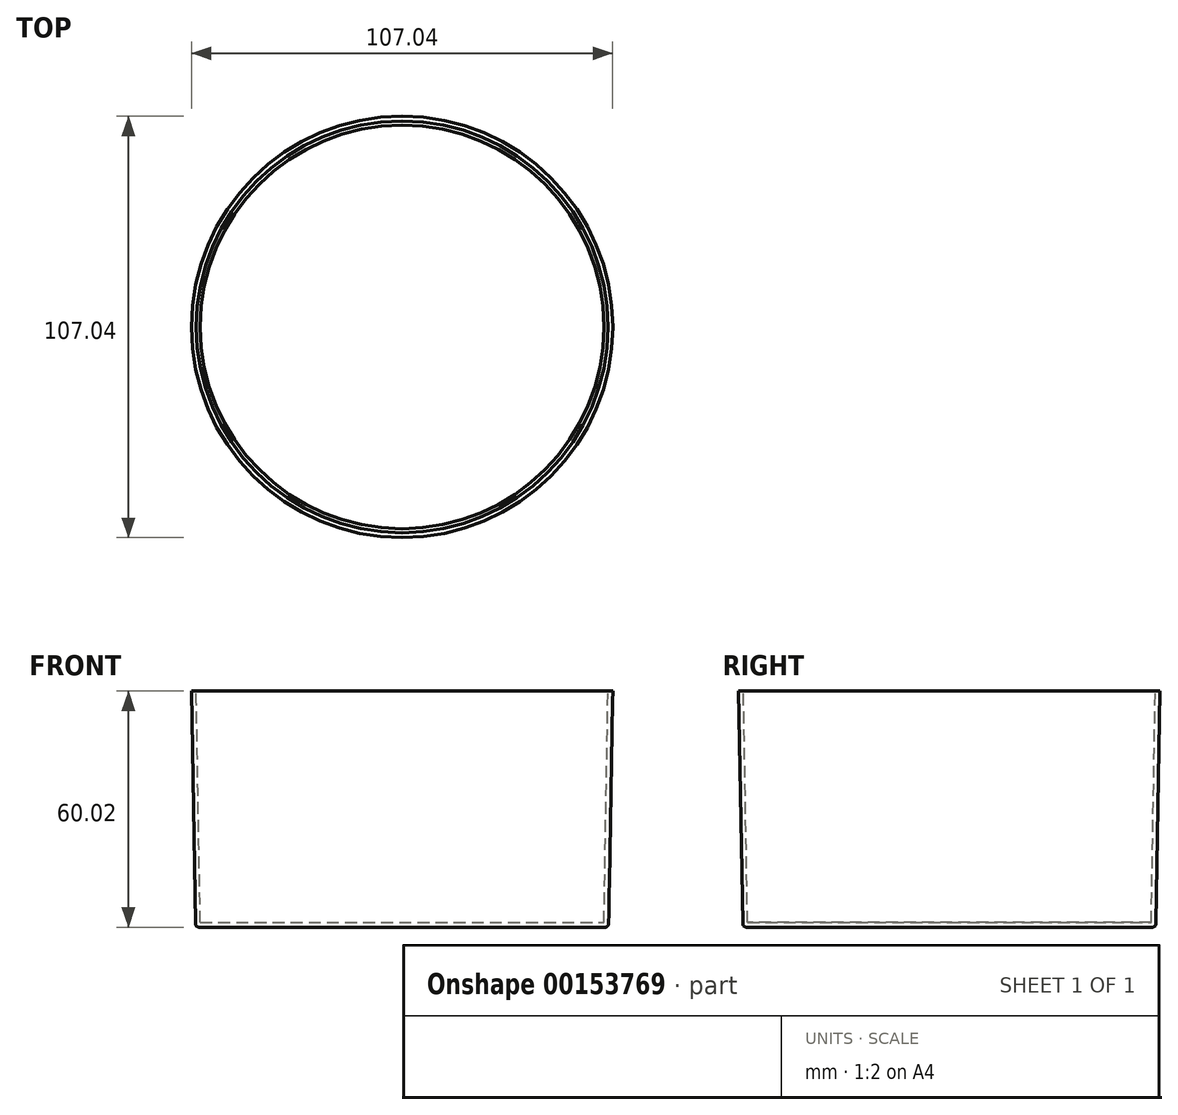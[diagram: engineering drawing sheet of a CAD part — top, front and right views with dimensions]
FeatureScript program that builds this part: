
annotation { "Feature Type Name" : "Feature", "Feature Type Description" : "" }
export const myFeature = defineFeature(function(context is Context, id is Id, definition is map)
    precondition{}
    {
        {
            var Q0;
            Q0=qCreatedBy(makeId("Front.planeOp"),FACE);
            var sketch = newSketch(context, id + "F0", { "sketchPlane" : qUnion([Q0])});
            skLineSegment(sketch, "E0", {"start": v(-52.47, 0) * mm, "end": v(0, 0) * mm});
            skLineSegment(sketch, "E1", {"start": v(0, 0) * mm, "end": v(0, 1.22) * mm});
            skLineSegment(sketch, "E2", {"start": v(0, 1.22) * mm, "end": v(-51.28, 1.22) * mm});
            skLineSegment(sketch, "E3", {"start": v(-51.28, 1.22) * mm, "end": v(-52.31, 60.02) * mm});
            skLineSegment(sketch, "E4", {"start": v(0, -33.65) * mm, "end": v(0, 1.22) * mm, "construction": true});
            skLineSegment(sketch, "E5.0", {"start": v(-52.47, 0) * mm, "end": v(-53.52, 60) * mm});
            skLineSegment(sketch, "E6", {"start": v(-52.31, 60.02) * mm, "end": v(-53.52, 60) * mm});
            skPoint(sketch, "E7.orphan", {"position": v(-18.71, 60.6) * mm});
            skSolve(sketch);
        }
        {
            var Q0;
            Q0 = qSketchRegion(id + "F0", true);
            var Q1;
            Q1=sQuery(id+"F0.wireOp",EDGE,"E4");
            revolve(context, id + "F1", {"entities" : qUnion([Q0]), "axis" : qUnion([Q1]), "revolveType" : RevolveType.FULL});
        }
        {
            var Q0;
            Q0=makeQuery(id+"F1.opRevolve","SWEPT_EDGE",EDGE,{"disambiguationData":[OSD([sQuery(id+"F0.wireOp",EDGE,"E0"),sQuery(id+"F0.wireOp",EDGE,"E5.0")])]});
            fillet(context, id + "F2", {"entities" : qUnion([Q0]), "radius" : 1 * mm, "tangentPropagation" : true, "allowEdgeOverflow" : false});
        }
    });
